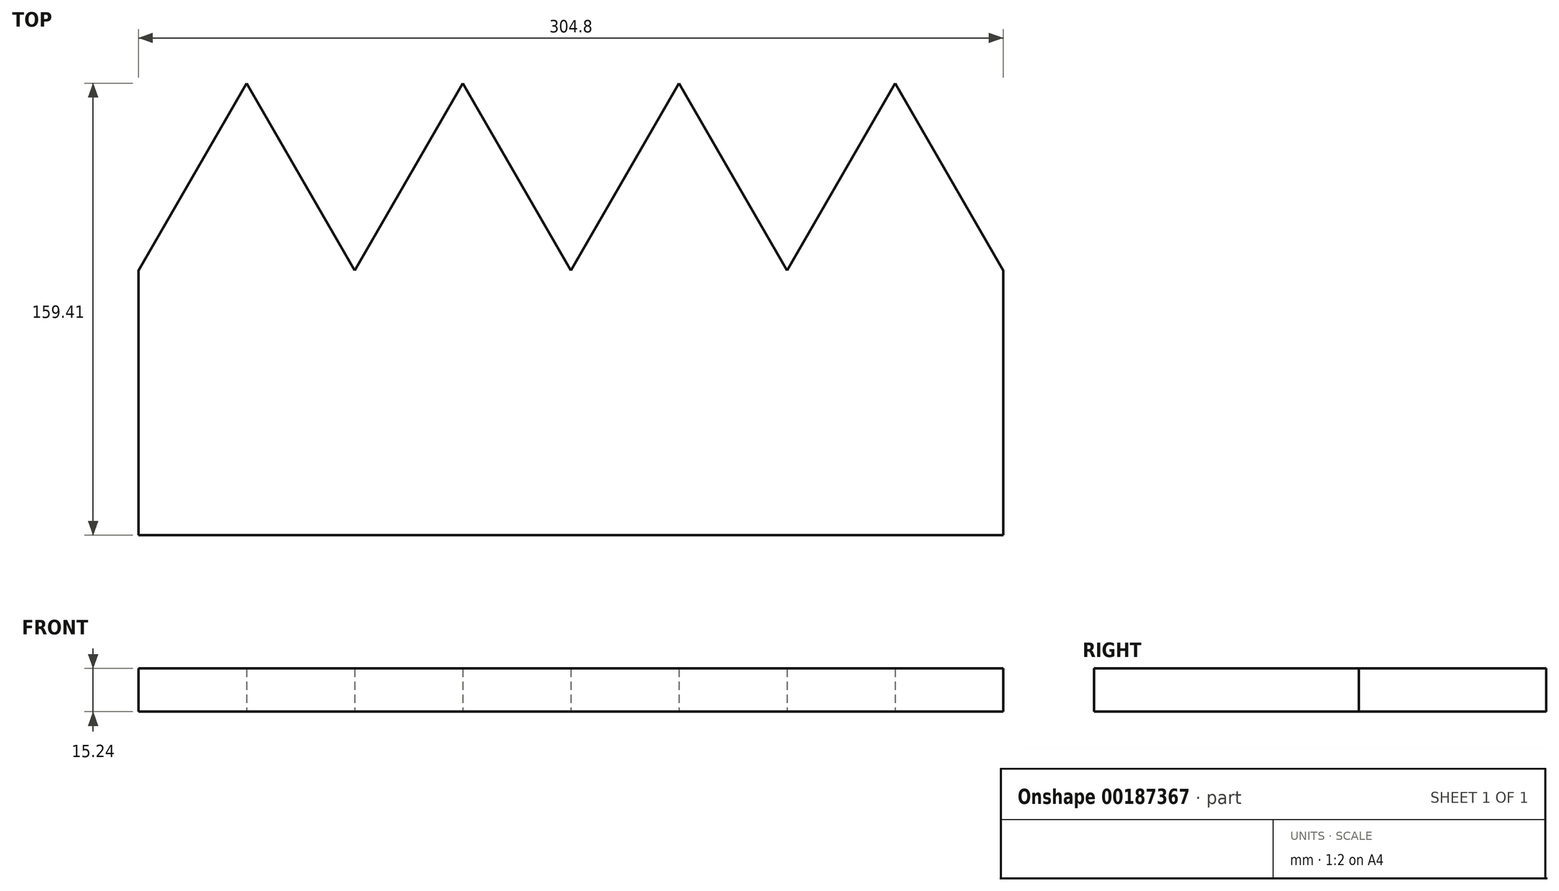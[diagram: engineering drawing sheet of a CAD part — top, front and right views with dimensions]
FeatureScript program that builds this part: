
annotation { "Feature Type Name" : "Feature", "Feature Type Description" : "" }
export const myFeature = defineFeature(function(context is Context, id is Id, definition is map)
    precondition{}
    {
        {
            var Q0;
            Q0=qCreatedBy(makeId("Top.planeOp"),FACE);
            var sketch = newSketch(context, id + "F0", { "sketchPlane" : qUnion([Q0])});
            skLineSegment(sketch, "E0", {"start": v(0, 0) * mm, "end": v(0, 93.42) * mm});
            skLineSegment(sketch, "E1", {"start": v(0, 93.42) * mm, "end": v(38.1, 159.4) * mm});
            skLineSegment(sketch, "E2", {"start": v(38.1, 159.4) * mm, "end": v(76.2, 93.42) * mm});
            skLineSegment(sketch, "E3", {"start": v(76.2, 93.42) * mm, "end": v(114.3, 159.4) * mm});
            skLineSegment(sketch, "E4", {"start": v(114.3, 159.4) * mm, "end": v(152.4, 93.42) * mm});
            skLineSegment(sketch, "E5", {"start": v(152.4, 93.42) * mm, "end": v(190.5, 159.4) * mm});
            skLineSegment(sketch, "E6", {"start": v(190.5, 159.4) * mm, "end": v(228.6, 93.42) * mm});
            skLineSegment(sketch, "E7", {"start": v(228.6, 93.42) * mm, "end": v(266.7, 159.4) * mm});
            skLineSegment(sketch, "E8", {"start": v(266.7, 159.4) * mm, "end": v(304.8, 93.42) * mm});
            skLineSegment(sketch, "E9", {"start": v(304.8, 93.42) * mm, "end": v(304.8, 0) * mm});
            skLineSegment(sketch, "E10", {"start": v(304.8, 0) * mm, "end": v(0, 0) * mm});
            skSolve(sketch);
        }
        {
            var Q0;
            Q0 = qSketchRegion(id + "F0", true);
            extrude(context, id + "F1", {"entities" : qUnion([Q0]), "depth" : 15.24 * mm});
        }
    });
